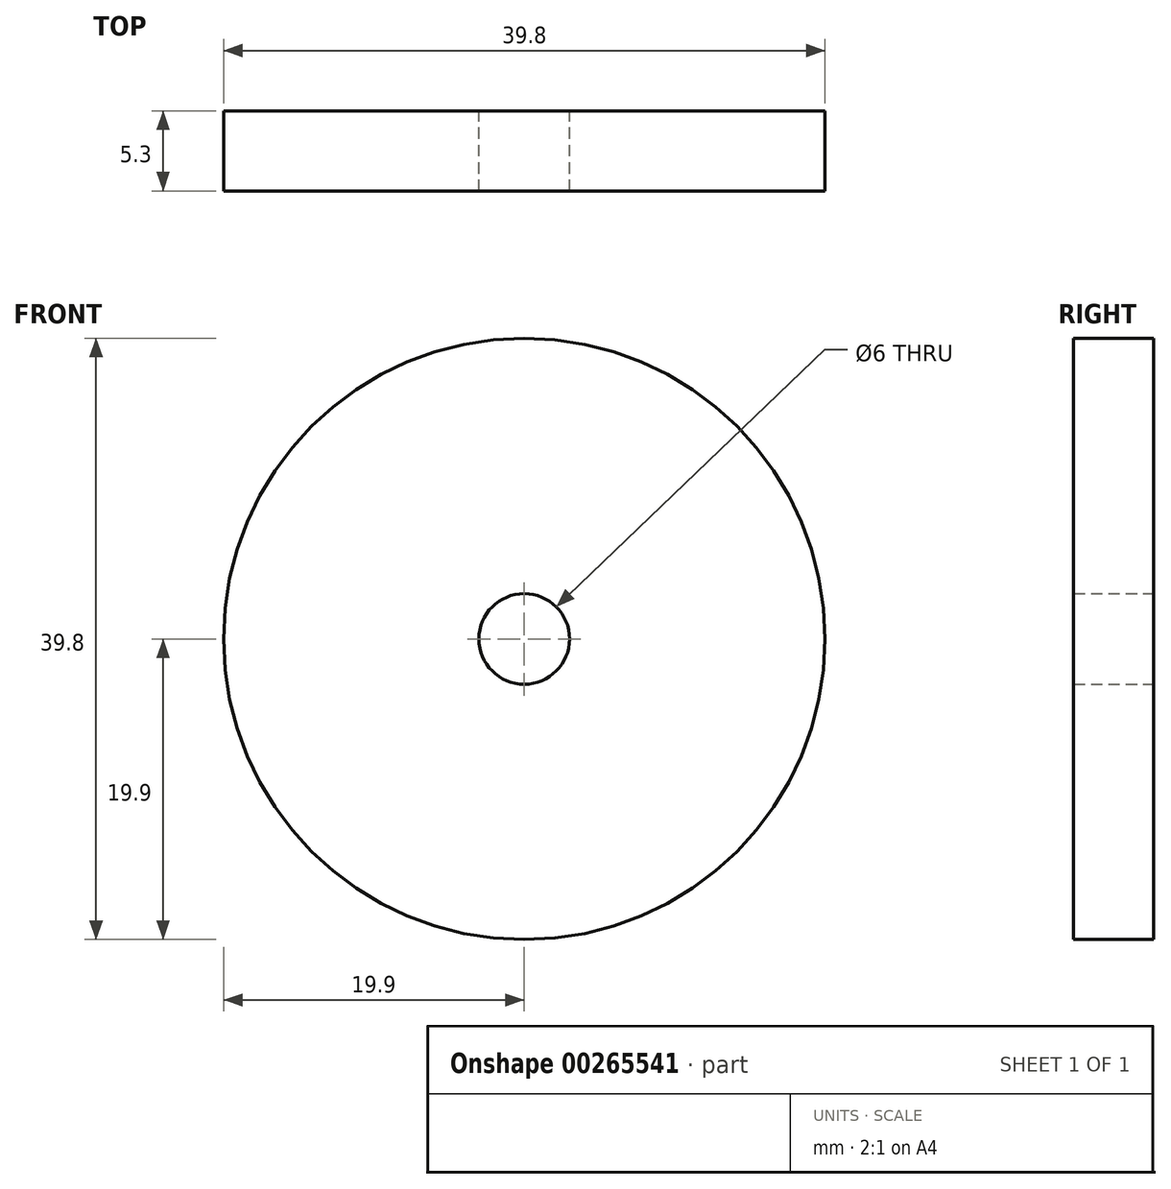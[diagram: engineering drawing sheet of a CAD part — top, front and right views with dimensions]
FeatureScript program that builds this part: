
annotation { "Feature Type Name" : "Feature", "Feature Type Description" : "" }
export const myFeature = defineFeature(function(context is Context, id is Id, definition is map)
    precondition{}
    {
        {
            var Q0;
            Q0=qCreatedBy(makeId("Front.planeOp"),FACE);
            var sketch = newSketch(context, id + "F0", { "sketchPlane" : qUnion([Q0])});
            skCircle(sketch, "E0", {"center": v(0, 0) * mm, "radius": 19.9 * mm});
            skCircle(sketch, "E1", {"center": v(0, 0) * mm, "radius": 3 * mm});
            skSolve(sketch);
        }
        {
            var Q0;
            Q0=makeQuery(id+"F0.imprint","IMPRINT",FACE,{"disambiguationData":[TD([[makeQuery(id+"F0.imprint","IMPRINT",EDGE,{"derivedFrom":sQuery(id+"F0.wireOp",EDGE,"E0")}),1.0]])]});
            extrude(context, id + "F1", {"entities" : qUnion([Q0]), "depth" : 5.3 * mm});
        }
    });
